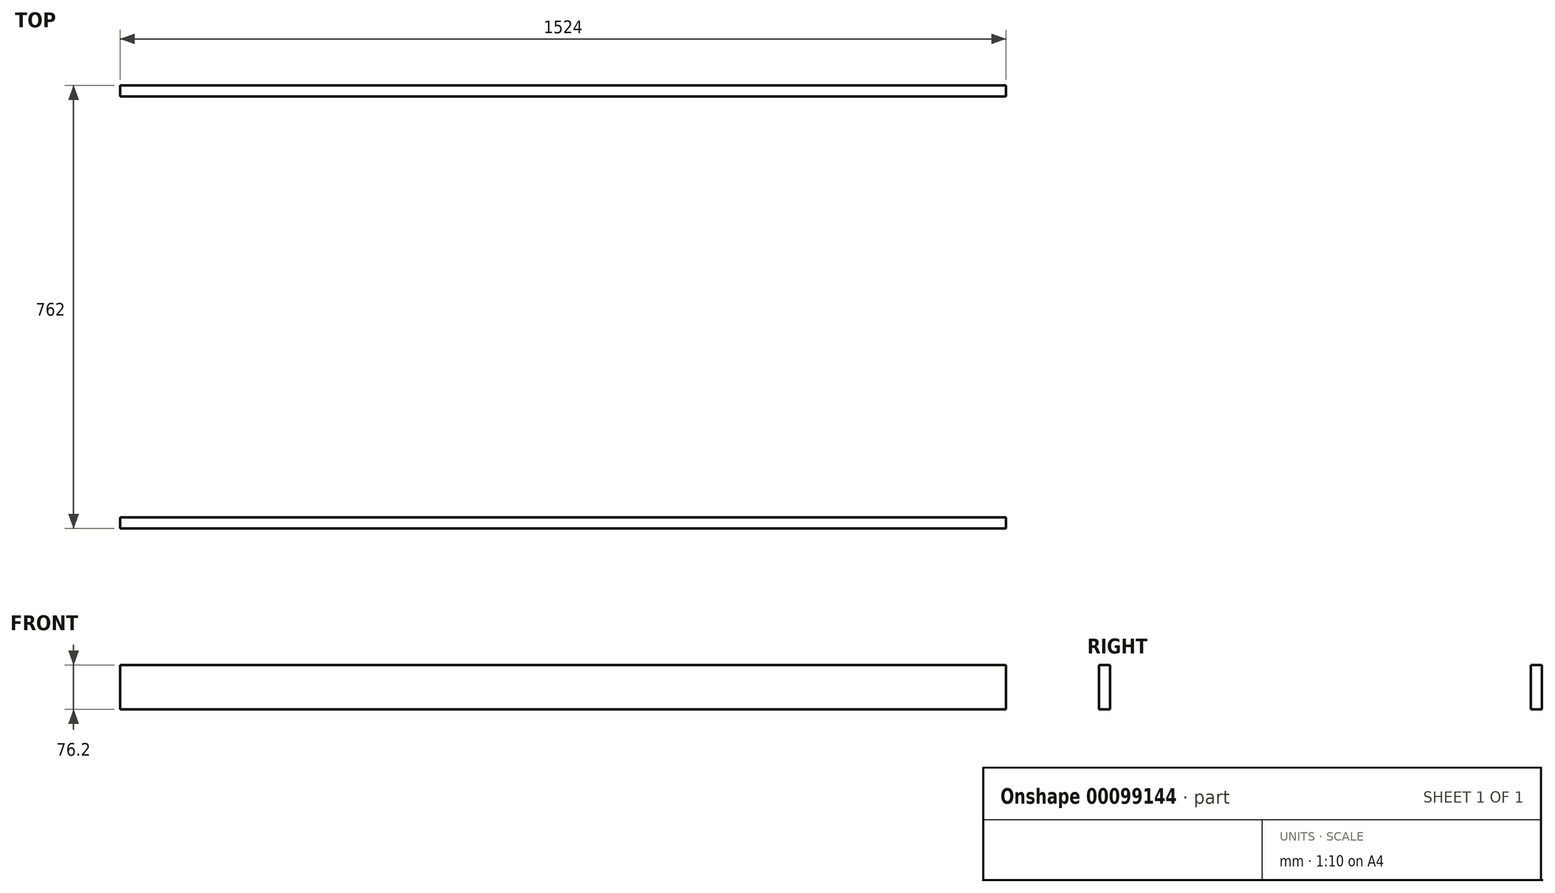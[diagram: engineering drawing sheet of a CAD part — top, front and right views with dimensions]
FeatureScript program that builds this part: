
annotation { "Feature Type Name" : "Feature", "Feature Type Description" : "" }
export const myFeature = defineFeature(function(context is Context, id is Id, definition is map)
    precondition{}
    {
        {
            var Q0;
            Q0=qCreatedBy(makeId("Top.planeOp"),FACE);
            var sketch = newSketch(context, id + "F0", { "sketchPlane" : qUnion([Q0])});
            skPoint(sketch, "E0", {"position": v(0, 381) * mm});
            skPoint(sketch, "E1", {"position": v(0, -381) * mm});
            skPoint(sketch, "E2", {"position": v(-762, 0) * mm});
            skPoint(sketch, "E3", {"position": v(762, 0) * mm});
            skPoint(sketch, "E4", {"position": v(-762, 381) * mm});
            skPoint(sketch, "E5", {"position": v(-762, -381) * mm});
            skPoint(sketch, "E6", {"position": v(762, 381) * mm});
            skPoint(sketch, "E7", {"position": v(762, -381) * mm});
            skLineSegment(sketch, "E8.bottom", {"start": v(-762, 381) * mm, "end": v(762, 381) * mm});
            skLineSegment(sketch, "E8.top", {"start": v(-762, 361.95) * mm, "end": v(762, 361.95) * mm});
            skLineSegment(sketch, "E8.left", {"start": v(-762, 381) * mm, "end": v(-762, 361.95) * mm});
            skLineSegment(sketch, "E8.right", {"start": v(762, 381) * mm, "end": v(762, 361.95) * mm});
            skLineSegment(sketch, "E9.bottom", {"start": v(-762, -381) * mm, "end": v(762, -381) * mm});
            skLineSegment(sketch, "E9.top", {"start": v(-762, -361.95) * mm, "end": v(762, -361.95) * mm});
            skLineSegment(sketch, "E9.left", {"start": v(-762, -381) * mm, "end": v(-762, -361.95) * mm});
            skLineSegment(sketch, "E9.right", {"start": v(762, -381) * mm, "end": v(762, -361.95) * mm});
            skLineSegment(sketch, "E10.bottom", {"start": v(-762, 361.95) * mm, "end": v(-742.95, 361.95) * mm});
            skLineSegment(sketch, "E10.top", {"start": v(-762, -361.95) * mm, "end": v(-742.95, -361.95) * mm});
            skLineSegment(sketch, "E10.left", {"start": v(-762, 361.95) * mm, "end": v(-762, -361.95) * mm});
            skLineSegment(sketch, "E10.right", {"start": v(-742.95, 361.95) * mm, "end": v(-742.95, -361.95) * mm});
            skLineSegment(sketch, "E11.bottom", {"start": v(762, 361.95) * mm, "end": v(742.95, 361.95) * mm});
            skLineSegment(sketch, "E11.top", {"start": v(762, -361.95) * mm, "end": v(742.95, -361.95) * mm});
            skLineSegment(sketch, "E11.left", {"start": v(762, 361.95) * mm, "end": v(762, -361.95) * mm});
            skLineSegment(sketch, "E11.right", {"start": v(742.95, 361.95) * mm, "end": v(742.95, -361.95) * mm});
            skSolve(sketch);
        }
        {
            var Q0;
            Q0=makeQuery(id+"F0.imprint","IMPRINT",FACE,{"disambiguationData":[TD([[makeQuery(id+"F0.imprint","IMPRINT",EDGE,{"derivedFrom":sQuery(id+"F0.wireOp",EDGE,"E8.bottom")}),-1.0]])]});
            var Q1;
            Q1=makeQuery(id+"F0.imprint","IMPRINT",FACE,{"disambiguationData":[TD([[makeQuery(id+"F0.imprint","IMPRINT",EDGE,{"derivedFrom":sQuery(id+"F0.wireOp",EDGE,"E10.bottom")}),-1.0]])]});
            var Q2;
            Q2=makeQuery(id+"F0.imprint","IMPRINT",FACE,{"disambiguationData":[TD([[makeQuery(id+"F0.imprint","IMPRINT",EDGE,{"derivedFrom":sQuery(id+"F0.wireOp",EDGE,"E9.bottom")}),1.0]])]});
            var Q3;
            Q3=makeQuery(id+"F0.imprint","IMPRINT",FACE,{"disambiguationData":[TD([[makeQuery(id+"F0.imprint","IMPRINT",EDGE,{"derivedFrom":sQuery(id+"F0.wireOp",EDGE,"E11.bottom")}),1.0]])]});
            extrude(context, id + "F1", {"entities" : qUnion([Q0, Q1, Q2, Q3]), "depth" : 76.2 * mm});
        }
    });
